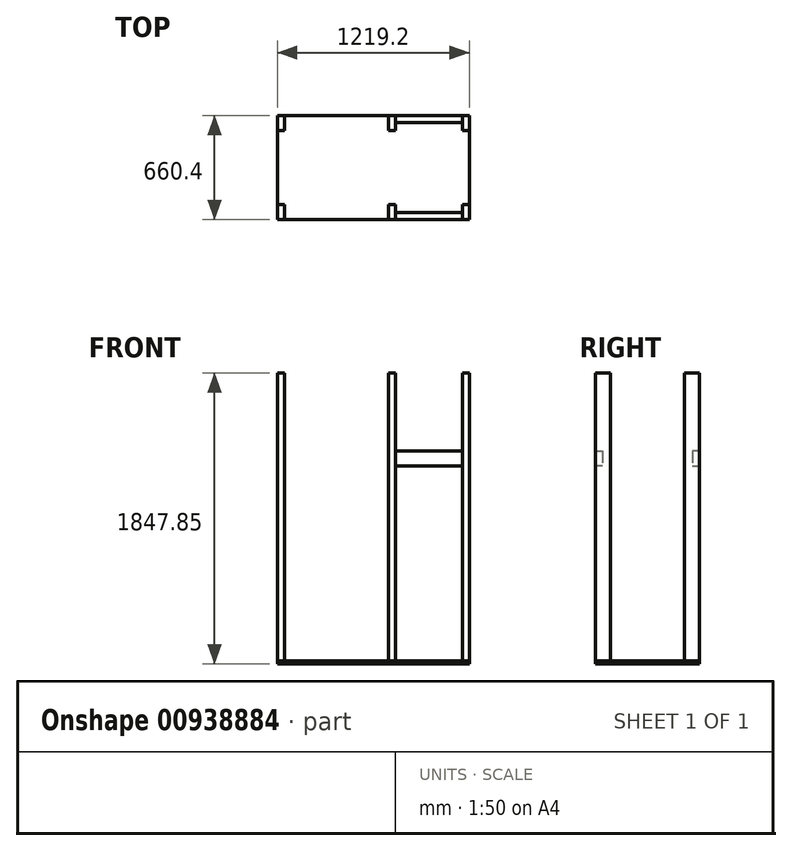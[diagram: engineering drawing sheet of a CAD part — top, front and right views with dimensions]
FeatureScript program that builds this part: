
annotation { "Feature Type Name" : "Feature", "Feature Type Description" : "" }
export const myFeature = defineFeature(function(context is Context, id is Id, definition is map)
    precondition{}
    {
        {
            var Q0;
            Q0=qCreatedBy(makeId("Top.planeOp"),FACE);
            var sketch = newSketch(context, id + "F0", { "sketchPlane" : qUnion([Q0])});
            skLineSegment(sketch, "E0.bottom", {"start": v(609.6, -330.2) * mm, "end": v(-609.6, -330.2) * mm});
            skLineSegment(sketch, "E0.top", {"start": v(609.6, 330.2) * mm, "end": v(-609.6, 330.2) * mm});
            skLineSegment(sketch, "E0.left", {"start": v(609.6, -330.2) * mm, "end": v(609.6, 330.2) * mm});
            skLineSegment(sketch, "E0.right", {"start": v(-609.6, -330.2) * mm, "end": v(-609.6, 330.2) * mm});
            skPoint(sketch, "E0.middle", {"position": v(0, 0) * mm});
            skSolve(sketch);
        }
        {
            var Q0;
            Q0=makeQuery(id+"F0.imprint","IMPRINT",FACE,{"disambiguationData":[TD([[makeQuery(id+"F0.imprint","IMPRINT",EDGE,{"derivedFrom":sQuery(id+"F0.wireOp",EDGE,"E0.bottom")}),-1.0]])]});
            extrude(context, id + "F1", {"entities" : qUnion([Q0]), "depth" : 19.05 * mm, "offsetDistance" : 25.4 * mm});
        }
        {
            var Q0;
            Q0=makeQuery(id+"F1.opExtrude","CAP_FACE",FACE,{"disambiguationData":[OSD([sQuery(id+"F0.wireOp",EDGE,"E0.bottom"),sQuery(id+"F0.wireOp",EDGE,"E0.top"),sQuery(id+"F0.wireOp",EDGE,"E0.left"),sQuery(id+"F0.wireOp",EDGE,"E0.right")])],"isStart":false});
            var sketch = newSketch(context, id + "F2", { "sketchPlane" : qUnion([Q0])});
            skLineSegment(sketch, "E1.bottom", {"start": v(-609.6, 330.2) * mm, "end": v(-565.15, 330.2) * mm});
            skLineSegment(sketch, "E1.top", {"start": v(-609.6, 234.95) * mm, "end": v(-565.15, 234.95) * mm});
            skLineSegment(sketch, "E1.left", {"start": v(-609.6, 330.2) * mm, "end": v(-609.6, 234.95) * mm});
            skLineSegment(sketch, "E1.right", {"start": v(-565.15, 330.2) * mm, "end": v(-565.15, 234.95) * mm});
            skLineSegment(sketch, "E2.bottom", {"start": v(-609.6, -330.2) * mm, "end": v(-565.15, -330.2) * mm});
            skLineSegment(sketch, "E2.top", {"start": v(-609.6, -234.95) * mm, "end": v(-565.15, -234.95) * mm});
            skLineSegment(sketch, "E2.left", {"start": v(-609.6, -330.2) * mm, "end": v(-609.6, -234.95) * mm});
            skLineSegment(sketch, "E2.right", {"start": v(-565.15, -330.2) * mm, "end": v(-565.15, -234.95) * mm});
            skLineSegment(sketch, "E3.bottom", {"start": v(609.6, -330.2) * mm, "end": v(565.15, -330.2) * mm});
            skLineSegment(sketch, "E3.top", {"start": v(609.6, -234.95) * mm, "end": v(565.15, -234.95) * mm});
            skLineSegment(sketch, "E3.left", {"start": v(609.6, -330.2) * mm, "end": v(609.6, -234.95) * mm});
            skLineSegment(sketch, "E3.right", {"start": v(565.15, -330.2) * mm, "end": v(565.15, -234.95) * mm});
            skLineSegment(sketch, "E4.bottom", {"start": v(609.6, 330.2) * mm, "end": v(565.15, 330.2) * mm});
            skLineSegment(sketch, "E4.top", {"start": v(609.6, 234.95) * mm, "end": v(565.15, 234.95) * mm});
            skLineSegment(sketch, "E4.left", {"start": v(609.6, 330.2) * mm, "end": v(609.6, 234.95) * mm});
            skLineSegment(sketch, "E4.right", {"start": v(565.15, 330.2) * mm, "end": v(565.15, 234.95) * mm});
            skLineSegment(sketch, "E5", {"start": v(95.25, 330.2) * mm, "end": v(95.25, 234.95) * mm});
            skLineSegment(sketch, "E6", {"start": v(95.25, -330.2) * mm, "end": v(95.25, -234.95) * mm});
            skPoint(sketch, "E6.endSnap0", {"position": v(587.38, -234.95) * mm});
            skLineSegment(sketch, "E7", {"start": v(95.25, -234.95) * mm, "end": v(139.7, -234.95) * mm});
            skLineSegment(sketch, "E8", {"start": v(139.7, -234.95) * mm, "end": v(139.7, -330.2) * mm});
            skLineSegment(sketch, "E9", {"start": v(95.25, 234.95) * mm, "end": v(139.7, 234.95) * mm});
            skLineSegment(sketch, "E10", {"start": v(139.7, 234.95) * mm, "end": v(139.7, 330.2) * mm});
            skSolve(sketch);
        }
        {
            var Q0;
            Q0=makeQuery(id+"F2.imprint","IMPRINT",FACE,{"disambiguationData":[TD([[makeQuery(id+"F2.imprint","IMPRINT",EDGE,{"derivedFrom":sQuery(id+"F2.wireOp",EDGE,"E1.bottom")}),1.0]])]});
            extrude(context, id + "F3", {"entities" : qUnion([Q0]), "depth" : 1828.8 * mm, "offsetDistance" : 25.4 * mm});
        }
        {
            var Q0;
            {var subQ0=sQuery(id+"F2.wireOp",EDGE,"E5");Q0=makeQuery(id+"F2.imprint","IMPRINT",FACE,{"disambiguationData":[TD([[makeQuery(id+"F2.imprint","IMPRINT",EDGE,{"derivedFrom":subQ0}),1.0]])]});}
            extrude(context, id + "F4", {"entities" : qUnion([Q0]), "depth" : 1828.8 * mm, "offsetDistance" : 25.4 * mm});
        }
        {
            var Q0;
            Q0=makeQuery(id+"F2.imprint","IMPRINT",FACE,{"disambiguationData":[TD([[makeQuery(id+"F2.imprint","IMPRINT",EDGE,{"derivedFrom":sQuery(id+"F2.wireOp",EDGE,"E4.bottom")}),1.0]])]});
            extrude(context, id + "F5", {"entities" : qUnion([Q0]), "depth" : 1828.8 * mm, "offsetDistance" : 25.4 * mm});
        }
        {
            var Q0;
            Q0=makeQuery(id+"F2.imprint","IMPRINT",FACE,{"disambiguationData":[TD([[makeQuery(id+"F2.imprint","IMPRINT",EDGE,{"derivedFrom":sQuery(id+"F2.wireOp",EDGE,"E2.bottom")}),-1.0]])]});
            extrude(context, id + "F6", {"entities" : qUnion([Q0]), "depth" : 1828.8 * mm, "offsetDistance" : 25.4 * mm});
        }
        {
            var Q0;
            {var subQ0=sQuery(id+"F2.wireOp",EDGE,"E6");Q0=makeQuery(id+"F2.imprint","IMPRINT",FACE,{"disambiguationData":[TD([[makeQuery(id+"F2.imprint","IMPRINT",EDGE,{"derivedFrom":subQ0}),-1.0]])]});}
            extrude(context, id + "F7", {"entities" : qUnion([Q0]), "depth" : 1828.8 * mm, "offsetDistance" : 25.4 * mm});
        }
        {
            var Q0;
            Q0=makeQuery(id+"F2.imprint","IMPRINT",FACE,{"disambiguationData":[TD([[makeQuery(id+"F2.imprint","IMPRINT",EDGE,{"derivedFrom":sQuery(id+"F2.wireOp",EDGE,"E3.bottom")}),-1.0]])]});
            extrude(context, id + "F8", {"entities" : qUnion([Q0]), "depth" : 1828.8 * mm, "offsetDistance" : 25.4 * mm});
        }
        {
            var Q0;
            Q0=makeQuery(id+"F7.opExtrude","SWEPT_FACE",FACE,{"disambiguationData":[OSD([sQuery(id+"F2.wireOp",EDGE,"E8")])]});
            var sketch = newSketch(context, id + "F9", { "sketchPlane" : qUnion([Q0])});
            skLineSegment(sketch, "E11", {"start": v(-330.2, 1352.55) * mm, "end": v(-285.75, 1352.55) * mm});
            skLineSegment(sketch, "E12", {"start": v(-285.75, 1352.55) * mm, "end": v(-285.75, 1257.3) * mm});
            skLineSegment(sketch, "E13", {"start": v(-285.75, 1257.3) * mm, "end": v(-330.2, 1257.3) * mm});
            skSolve(sketch);
        }
        {
            var Q0;
            {var subQ0=sQuery(id+"F9.wireOp",EDGE,"E11");Q0=makeQuery(id+"F9.imprint","IMPRINT",FACE,{"disambiguationData":[TD([[makeQuery(id+"F9.imprint","IMPRINT",EDGE,{"derivedFrom":subQ0}),-1.0]])]});}
            extrude(context, id + "F10", {"entities" : qUnion([Q0]), "depth" : 425.45 * mm, "offsetDistance" : 25.4 * mm});
        }
        {
            var Q0;
            Q0=makeQuery(id+"F4.opExtrude","SWEPT_FACE",FACE,{"disambiguationData":[OSD([sQuery(id+"F2.wireOp",EDGE,"E10")])]});
            var sketch = newSketch(context, id + "F11", { "sketchPlane" : qUnion([Q0])});
            skLineSegment(sketch, "E14", {"start": v(330.2, 1352.55) * mm, "end": v(285.75, 1352.55) * mm});
            skLineSegment(sketch, "E15", {"start": v(285.75, 1352.55) * mm, "end": v(285.75, 1257.3) * mm});
            skLineSegment(sketch, "E16", {"start": v(285.75, 1257.3) * mm, "end": v(330.2, 1257.3) * mm});
            skSolve(sketch);
        }
        {
            var Q0;
            {var subQ0=sQuery(id+"F11.wireOp",EDGE,"E14");Q0=makeQuery(id+"F11.imprint","IMPRINT",FACE,{"disambiguationData":[TD([[makeQuery(id+"F11.imprint","IMPRINT",EDGE,{"derivedFrom":subQ0}),1.0]])]});}
            extrude(context, id + "F12", {"entities" : qUnion([Q0]), "depth" : 425.45 * mm, "offsetDistance" : 25.4 * mm});
        }
    });
